# Revit family: rba-bim-rba4005 Series
name_source: partatom
category: Plumbing Fixtures
revit_build: Autodesk Revit 2018 (Build: 20170223_1515(x64)
units: mm (PartAtom-declared; Revit-internal decimal feet)

## family parameters
Always vertical = Yes
Cut with Voids When Loaded = No
Part Type = Normal
Room Calculation Point = No
Round Connector Dimension = Use Diameter
Shared = No
Work Plane-Based = No

## types (9) — shared parameters
Diameter = 32 mm  [stored 0.104987 ft]
Manufacturer = RBA Group
Materials and Finishes = Stainless Steel Matte Black Finish

## per-type parameters (varying)
| type | Lgth | Model | Modified Issue | URL |
| Straight Grab Rail 300mm | 300 mm  [stored 0.984252 ft] | RBA4005-030 | 20211007.01 | www.rba.com.au |
| Straight Grab Rail 450mm | 450 mm | RBA4005-045 | 20211007.01 | www.rba.com.au |
| Straight Grab Rail 600mm | 600 mm | RBA4005-060 | 20191004.01 | www.rba.com.au |
| Straight Grab Rail 750mm | 750 mm | RBA4000-075 | 20191004.01 | http://www.rba.com.au |
| Straight Grab Rail 900mm | 900 mm | RBA4005-090 | 20211007.01 | www.rba.com.au |
| Straight Grab Rail 800mm | 800 mm | RBA4000-080 | 20191004.01 | http://www.rba.com.au |
| Straight Grab Rail 1000mm | 1000 mm  [stored 3.28084 ft] | RBA4000-100 | 20191004.01 | http://www.rba.com.au |
| Straight Grab Rail 1200mm | 1200 mm | RBA4000-120 | 20191004.01 | http://www.rba.com.au |
| Straight Grab Rail 400mm | 400 mm | RBA4000-040 | 20191108.1 | www.rba.com.au |

note: column(s) folded — value = type name in every type: Description

note: [stored X ft] marks values corroborated as IEEE doubles in the binary element streams (Revit-internal decimal feet)

## geometry (parser evidence)
native form markers: Sweep x3
no freeform markers — native parametric forms only
